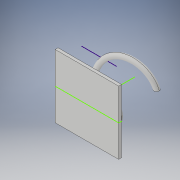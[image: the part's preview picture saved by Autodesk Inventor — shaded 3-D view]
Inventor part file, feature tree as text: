
AUTODESK INVENTOR PART (.ipt)
format: ipt  version: 2019 (Build 230136000, 136)  size: 242,176 bytes
history: native  units: mm
features: sketch x1, helix x1, extrude x1
ambient origin geometry x8: Origin, YZ Plane, XZ Plane, XY Plane, X Axis, Y Axis, Z Axis, Center Point
bodies: Solid1 (feature_tree)
feature tree (3):
  sketch  "Sketch1"  dims[d1=4.0mm d6=2.0mm d7=4.0mm d8=10.0mm d9=0.174533mm d10=90.0deg d11=90.0deg d12=0.0mm d13=0.0mm d15=6.0mm d16=0.0mm d18=3.0mm d20=3.0mm d21=2.0mm]
  helix  "Coil1"  [1 undecoded]
  extrude  "Extrusion1"  Depth=6.0mm TaperAngle=0.0deg
note: 1 required parameter value undecoded (feature->parameter linkage not recoverable at this tier; creation-order binding heuristic only, values carry confidence <= 0.55)
